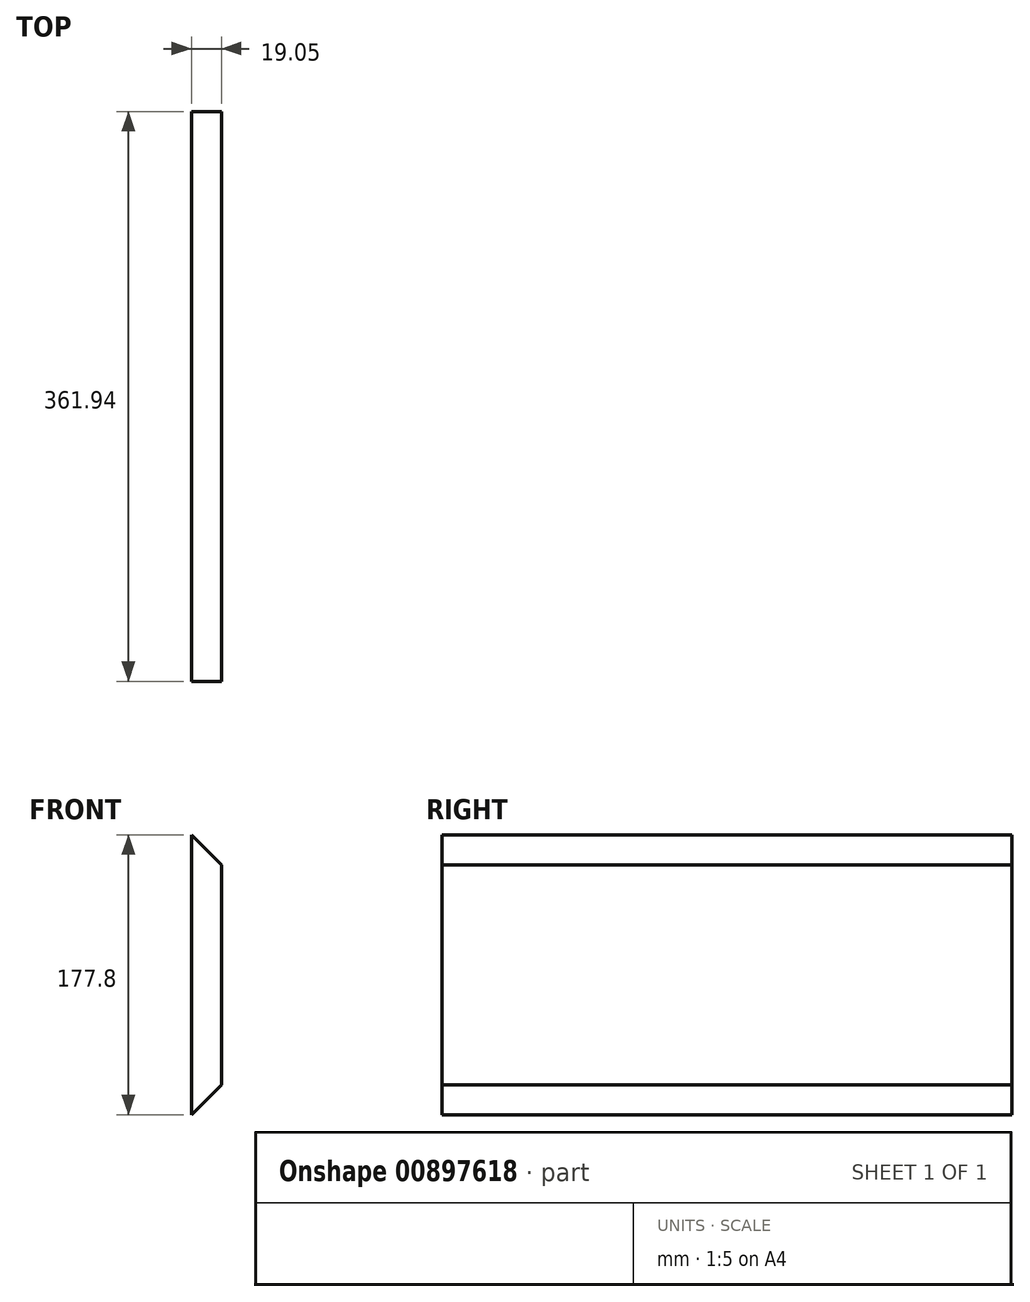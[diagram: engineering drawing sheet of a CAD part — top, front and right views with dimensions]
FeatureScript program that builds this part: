
annotation { "Feature Type Name" : "Feature", "Feature Type Description" : "" }
export const myFeature = defineFeature(function(context is Context, id is Id, definition is map)
    precondition{}
    {
        {
            var Q0;
            Q0=qCreatedBy(makeId("Right.planeOp"),FACE);
            var sketch = newSketch(context, id + "F0", { "sketchPlane" : qUnion([Q0])});
            skLineSegment(sketch, "E0.bottom", {"start": v(-180.97, -88.9) * mm, "end": v(180.98, -88.9) * mm});
            skLineSegment(sketch, "E0.top", {"start": v(-180.97, 88.9) * mm, "end": v(180.97, 88.9) * mm});
            skLineSegment(sketch, "E0.left", {"start": v(-180.97, -88.9) * mm, "end": v(-180.98, 88.9) * mm});
            skLineSegment(sketch, "E0.right", {"start": v(180.98, -88.9) * mm, "end": v(180.97, 88.9) * mm});
            skPoint(sketch, "E0.middle", {"position": v(0, 0) * mm});
            skSolve(sketch);
        }
        {
            var Q0;
            Q0=makeQuery(id+"F0.imprint","IMPRINT",FACE,{"disambiguationData":[TD([[makeQuery(id+"F0.imprint","IMPRINT",EDGE,{"derivedFrom":sQuery(id+"F0.wireOp",EDGE,"E0.bottom")}),1.0]])]});
            extrude(context, id + "F1", {"entities" : qUnion([Q0]), "depth" : 19.05 * mm, "offsetDistance" : 25.4 * mm});
        }
        {
            var Q0;
            Q0=makeQuery(id+"F1.opExtrude","CAP_EDGE",EDGE,{"disambiguationData":[OSD([sQuery(id+"F0.wireOp",EDGE,"E0.top")])],"isStart":false});
            var Q1;
            Q1=makeQuery(id+"F1.opExtrude","CAP_EDGE",EDGE,{"disambiguationData":[OSD([sQuery(id+"F0.wireOp",EDGE,"E0.bottom")])],"isStart":false});
            chamfer(context, id + "F2", {"entities" : qUnion([Q0, Q1]), "width" : 19.05 * mm, "tangentPropagation" : true});
        }
    });
